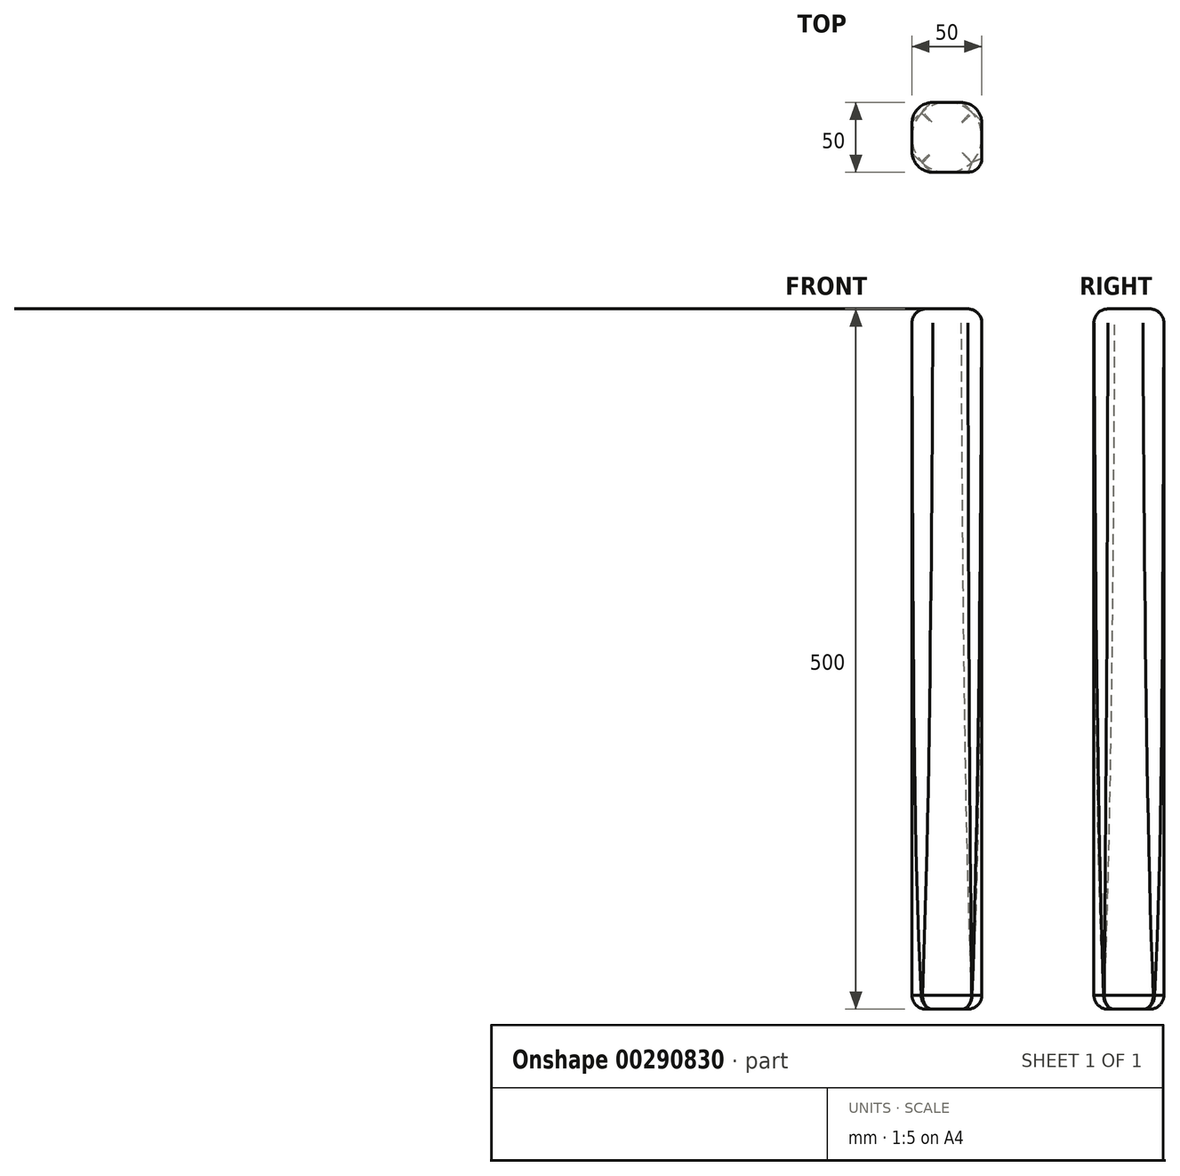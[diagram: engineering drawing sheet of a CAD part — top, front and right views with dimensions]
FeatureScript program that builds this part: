
annotation { "Feature Type Name" : "Feature", "Feature Type Description" : "" }
export const myFeature = defineFeature(function(context is Context, id is Id, definition is map)
    precondition{}
    {
        {
            var Q0;
            Q0=qCreatedBy(makeId("Top.planeOp"),FACE);
            cPlane(context, id + "F0", {"entities" : qUnion([Q0]), "cplaneType" : CPlaneType.OFFSET, "offset" : 500 * mm, "width" : 150 * mm, "height" : 150 * mm});
        }
        {
            var Q0;
            Q0=qCreatedBy(id+"F0.planeOp",FACE);
            var sketch = newSketch(context, id + "F1", { "sketchPlane" : qUnion([Q0])});
            skLineSegment(sketch, "E0.bottom", {"start": v(25, 25) * mm, "end": v(-25, 25) * mm});
            skLineSegment(sketch, "E0.top", {"start": v(25, -25) * mm, "end": v(-25, -25) * mm});
            skLineSegment(sketch, "E0.left", {"start": v(25, 25) * mm, "end": v(25, -25) * mm});
            skLineSegment(sketch, "E0.right", {"start": v(-25, 25) * mm, "end": v(-25, -25) * mm});
            skPoint(sketch, "E0.middle", {"position": v(0, 0) * mm});
            skSolve(sketch);
        }
        {
            var Q0;
            Q0=qCreatedBy(makeId("Top.planeOp"),FACE);
            var sketch = newSketch(context, id + "F2", { "sketchPlane" : qUnion([Q0])});
            skCircle(sketch, "E1", {"center": v(0, 0) * mm, "radius": 25 * mm});
            skSolve(sketch);
        }
        {
            var Q0;
            Q0=makeQuery(id+"F1.imprint","IMPRINT",FACE,{"disambiguationData":[TD([[makeQuery(id+"F1.imprint","IMPRINT",EDGE,{"derivedFrom":sQuery(id+"F1.wireOp",EDGE,"E0.bottom")}),1.0]])]});
            var Q1;
            Q1=makeQuery(id+"F2.imprint","IMPRINT",FACE,{"disambiguationData":[TD([[makeQuery(id+"F2.imprint","IMPRINT",EDGE,{"derivedFrom":sQuery(id+"F2.wireOp",EDGE,"E1")}),1.0]])]});
            loft(context, id + "F3", {"sheetProfilesArray" : [{ "sheetProfileEntities" : qUnion([Q0]) }, { "sheetProfileEntities" : qUnion([Q1]) }]});
        }
        {
            var Q0;
            Q0=makeQuery(id+"F3.opLoft","SWEPT_EDGE",EDGE,{"disambiguationData":[OSD([sQuery(id+"F1.wireOp",EDGE,"E0.bottom"),sQuery(id+"F1.wireOp",EDGE,"E0.top"),sQuery(id+"F1.wireOp",EDGE,"E0.right"),sQuery(id+"F2.wireOp",EDGE,"E1")])]});
            var Q1;
            Q1=makeQuery(id+"F3.opLoft","SWEPT_EDGE",EDGE,{"disambiguationData":[OSD([sQuery(id+"F1.wireOp",EDGE,"E0.top"),sQuery(id+"F1.wireOp",EDGE,"E0.left"),sQuery(id+"F1.wireOp",EDGE,"E0.right"),sQuery(id+"F2.wireOp",EDGE,"E1")])]});
            var Q2;
            Q2=makeQuery(id+"F3.opLoft","SWEPT_EDGE",EDGE,{"disambiguationData":[OSD([sQuery(id+"F1.wireOp",EDGE,"E0.bottom"),sQuery(id+"F1.wireOp",EDGE,"E0.top"),sQuery(id+"F1.wireOp",EDGE,"E0.left"),sQuery(id+"F2.wireOp",EDGE,"E1")])]});
            var Q3;
            Q3=makeQuery(id+"F3.opLoft","SWEPT_EDGE",EDGE,{"disambiguationData":[OSD([sQuery(id+"F1.wireOp",EDGE,"E0.bottom"),sQuery(id+"F1.wireOp",EDGE,"E0.left")])]});
            fillet(context, id + "F4", {"entities" : qUnion([Q0, Q1, Q2, Q3]), "radius" : 15 * mm, "tangentPropagation" : true, "allowEdgeOverflow" : false});
        }
        {
            var Q0;
            Q0=makeQuery(id+"F3.opLoft","MID_CAP_EDGE",EDGE,{"disambiguationData":[OSD([sQuery(id+"F1.wireOp",EDGE,"E0.bottom"),sQuery(id+"F1.wireOp",EDGE,"E0.top"),sQuery(id+"F1.wireOp",EDGE,"E0.left"),sQuery(id+"F2.wireOp",EDGE,"E1")])],"capPos":1.0});
            var Q1;
            Q1=makeQuery(id+"F3.opLoft","SWEPT_FACE",FACE,{"disambiguationData":[OSD([sQuery(id+"F1.wireOp",EDGE,"E0.bottom"),sQuery(id+"F1.wireOp",EDGE,"E0.top"),sQuery(id+"F1.wireOp",EDGE,"E0.left"),sQuery(id+"F2.wireOp",EDGE,"E1")])]});
            var Q2;
            Q2=makeQuery(id+"F3.opLoft","MID_CAP_EDGE",EDGE,{"disambiguationData":[OSD([sQuery(id+"F1.wireOp",EDGE,"E0.bottom"),sQuery(id+"F1.wireOp",EDGE,"E0.top"),sQuery(id+"F1.wireOp",EDGE,"E0.left"),sQuery(id+"F1.wireOp",EDGE,"E0.right"),sQuery(id+"F2.wireOp",EDGE,"E1")])],"capPos":1.0});
            var Q3;
            Q3=makeQuery(id+"F3.opLoft","MID_CAP_EDGE",EDGE,{"disambiguationData":[OSD([sQuery(id+"F1.wireOp",EDGE,"E0.top"),sQuery(id+"F1.wireOp",EDGE,"E0.left"),sQuery(id+"F1.wireOp",EDGE,"E0.right"),sQuery(id+"F2.wireOp",EDGE,"E1")])],"capPos":1.0});
            fillet(context, id + "F5", {"entities" : qUnion([Q0, Q1, Q2, Q3]), "radius" : 10 * mm, "tangentPropagation" : true, "allowEdgeOverflow" : false});
        }
    });
